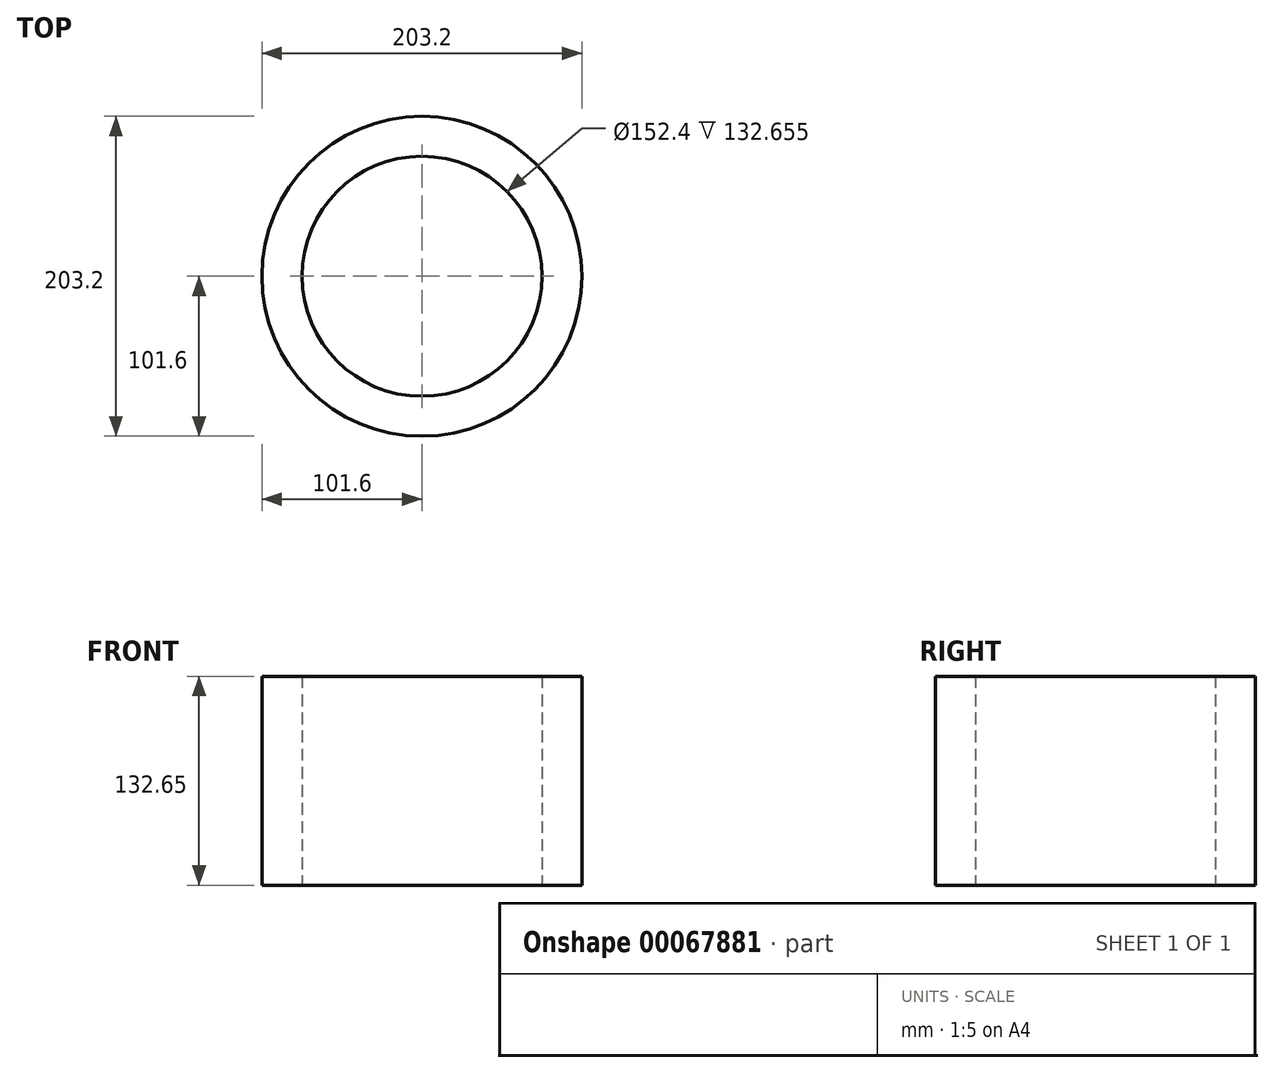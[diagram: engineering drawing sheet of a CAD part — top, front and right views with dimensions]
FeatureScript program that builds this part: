
annotation { "Feature Type Name" : "Feature", "Feature Type Description" : "" }
export const myFeature = defineFeature(function(context is Context, id is Id, definition is map)
    precondition{}
    {
        {
            var Q0;
            Q0=qCreatedBy(makeId("Top.planeOp"),FACE);
            var sketch = newSketch(context, id + "F0", { "sketchPlane" : qUnion([Q0])});
            skCircle(sketch, "E0", {"center": v(0, 0) * mm, "radius": 101.6 * mm});
            skCircle(sketch, "E1", {"center": v(0, 0) * mm, "radius": 76.2 * mm});
            skSolve(sketch);
        }
        {
            var Q0;
            Q0 = qSketchRegion(id + "F0", true);
            extrude(context, id + "F1", {"entities" : qUnion([Q0]), "depth" : 132.65 * mm});
        }
    });
